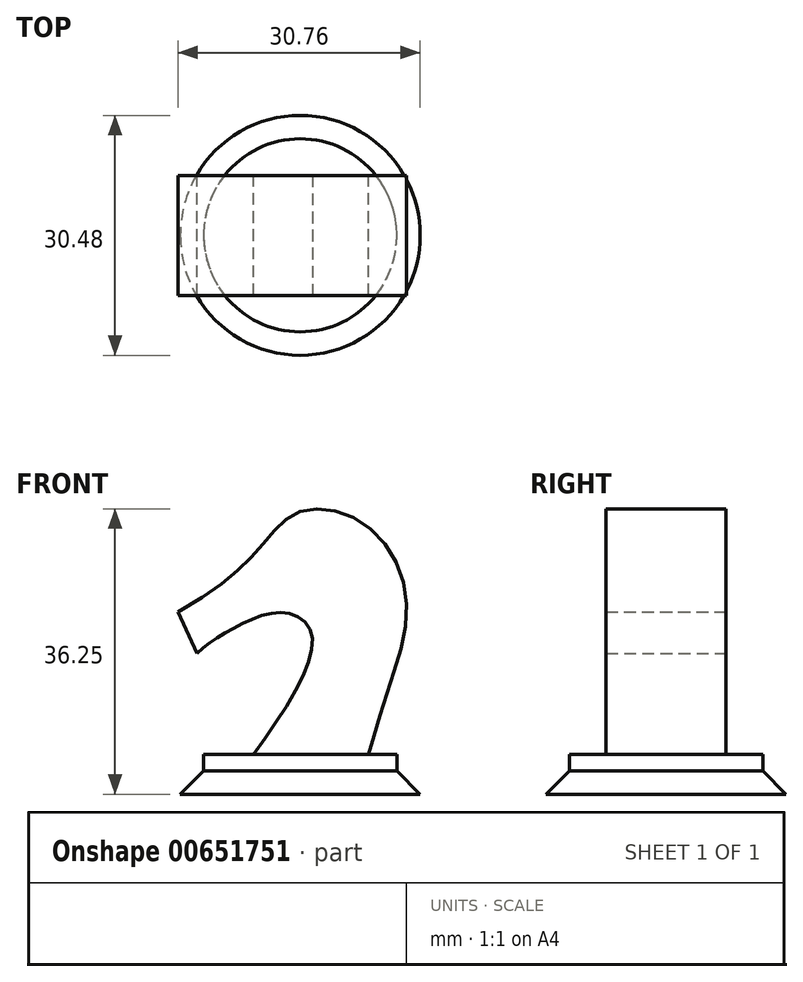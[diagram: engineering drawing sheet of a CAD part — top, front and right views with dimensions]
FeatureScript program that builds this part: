
annotation { "Feature Type Name" : "Feature", "Feature Type Description" : "" }
export const myFeature = defineFeature(function(context is Context, id is Id, definition is map)
    precondition{}
    {
        {
            var Q0;
            Q0=qCreatedBy(makeId("Front.planeOp"),FACE);
            var sketch = newSketch(context, id + "F0", { "sketchPlane" : qUnion([Q0])});
            skLineSegment(sketch, "E0", {"start": v(0, 0) * mm, "end": v(-15.24, 0) * mm});
            skLineSegment(sketch, "E1", {"start": v(0, 0) * mm, "end": v(0, 5.08) * mm});
            skLineSegment(sketch, "E2", {"start": v(-15.24, 0) * mm, "end": v(-12.27, 2.97) * mm});
            skLineSegment(sketch, "E3", {"start": v(-12.27, 2.97) * mm, "end": v(-12.27, 5.08) * mm});
            skLineSegment(sketch, "E4", {"start": v(-12.27, 5.08) * mm, "end": v(0, 5.08) * mm});
            skSolve(sketch);
        }
        {
            var Q0;
            Q0 = qSketchRegion(id + "F0", true);
            var Q1;
            Q1=sQuery(id+"F0.wireOp",EDGE,"E1");
            revolve(context, id + "F1", {"entities" : qUnion([Q0]), "axis" : qUnion([Q1]), "revolveType" : RevolveType.FULL});
        }
        {
            var Q0;
            Q0=qCreatedBy(makeId("Front.planeOp"),FACE);
            var sketch = newSketch(context, id + "F2", { "sketchPlane" : qUnion([Q0])});
            skLineSegment(sketch, "E5", {"start": v(0, 3.37) * mm, "end": v(-7.34, 3.17) * mm});
            skLineSegment(sketch, "E6", {"start": v(0, 3.37) * mm, "end": v(7.24, 2.15) * mm});
            skFitSpline(sketch, "E7", {"points": [v(7.24, 2.15) * mm, v(10.27, 10.57) * mm, v(13.51, 24.01) * mm, v(8.47, 34.1) * mm, v(0, 35.9) * mm, v(-5.33, 31.1) * mm, v(-15.52, 23.17) * mm], "startDerivative": vector(27.07, 34) * mm, "endDerivative": vector(-82.94, -45.24) * mm});
            skLineSegment(sketch, "E8", {"start": v(-15.52, 23.17) * mm, "end": v(-13.13, 17.9) * mm});
            skFitSpline(sketch, "E9", {"points": [v(-13.13, 17.9) * mm, v(-8.57, 21.01) * mm, v(-2.09, 23.05) * mm, v(1.51, 19.93) * mm, v(-7.34, 3.17) * mm], "startDerivative": vector(17.07, 16.36) * mm, "endDerivative": vector(-34.65, -46.04) * mm});
            skSolve(sketch);
        }
        {
            var Q0;
            Q0 = qSketchRegion(id + "F2", true);
            extrude(context, id + "F3", {"entities" : qUnion([Q0]), "operationType" : NewBodyOperationType.ADD, "depth" : 7.62 * mm, "offsetDistance" : 25.4 * mm, "hasSecondDirection" : true, "secondDirectionOppositeDirection" : true, "secondDirectionDepth" : 7.62 * mm});
        }
    });
